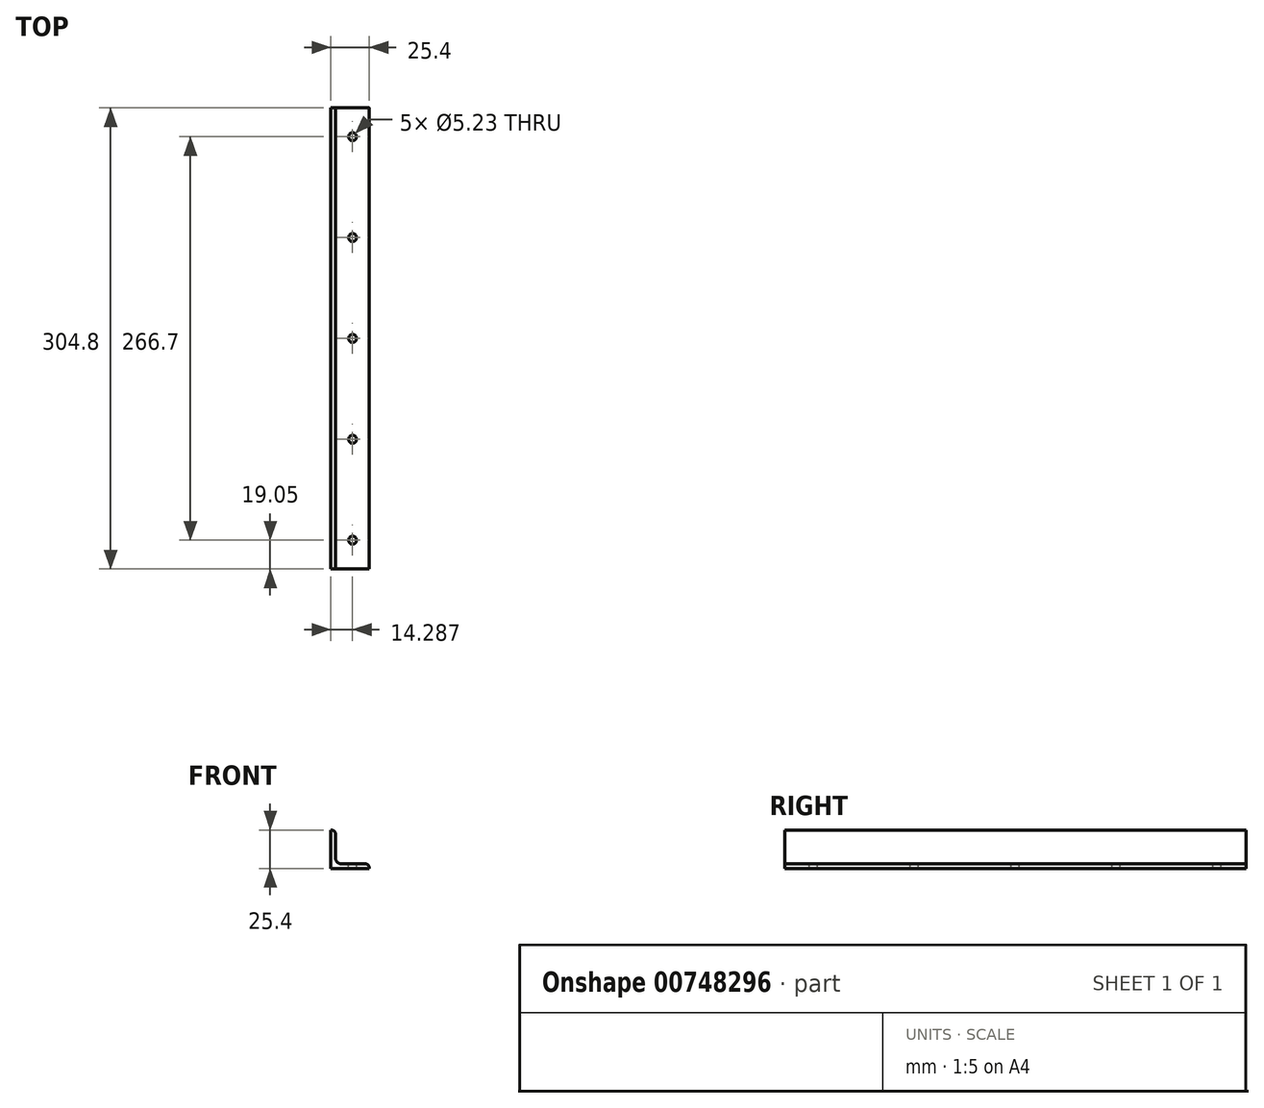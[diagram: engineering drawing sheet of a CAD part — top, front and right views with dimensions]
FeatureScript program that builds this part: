
annotation { "Feature Type Name" : "Feature", "Feature Type Description" : "" }
export const myFeature = defineFeature(function(context is Context, id is Id, definition is map)
    precondition{}
    {
        {
            var Q0;
            Q0=qCreatedBy(makeId("Front.planeOp"),FACE);
            var sketch = newSketch(context, id + "F0", { "sketchPlane" : qUnion([Q0])});
            skLineSegment(sketch, "E0", {"start": v(0, 0) * mm, "end": v(-25.4, 0) * mm});
            skLineSegment(sketch, "E1", {"start": v(-25.4, 0) * mm, "end": v(-25.4, 25.4) * mm});
            skLineSegment(sketch, "E2", {"start": v(-25.4, 25.4) * mm, "end": v(-25.4, 25.4) * mm});
            skLineSegment(sketch, "E3", {"start": v(-22.23, 22.23) * mm, "end": v(-22.23, 6.35) * mm});
            skLineSegment(sketch, "E4", {"start": v(-19.05, 3.18) * mm, "end": v(-3.18, 3.18) * mm});
            skLineSegment(sketch, "E5", {"start": v(0, 0) * mm, "end": v(0, 0) * mm});
            skPoint(sketch, "E6.visualSharp", {"position": v(-22.23, 3.18) * mm});
            skArc(sketch, "E6.filletArc", {"start": v(-22.23, 6.35) * mm, "mid": v(-21.3, 4.1) * mm, "end": v(-19.05, 3.18) * mm});
            skPoint(sketch, "E7.visualSharp", {"position": v(-22.23, 25.4) * mm});
            skArc(sketch, "E7.filletArc", {"start": v(-22.23, 22.23) * mm, "mid": v(-23.15, 24.47) * mm, "end": v(-25.4, 25.4) * mm});
            skPoint(sketch, "E8.visualSharp", {"position": v(0, 3.18) * mm});
            skArc(sketch, "E8.filletArc", {"start": v(0, 0) * mm, "mid": v(-0.93, 2.25) * mm, "end": v(-3.18, 3.18) * mm});
            skSolve(sketch);
        }
        {
            var Q0;
            Q0=qSketchRegion(id+"F0",true);
            extrude(context, id + "F1", {"entities" : qUnion([Q0]), "depth" : 304.8 * mm, "offsetDistance" : 25.4 * mm});
        }
        {
            var Q0;
            Q0=makeQuery(id+"F1.opExtrude","SWEPT_FACE",FACE,{"disambiguationData":[OSD([sQuery(id+"F0.wireOp",EDGE,"E4")])]});
            var sketch = newSketch(context, id + "F2", { "sketchPlane" : qUnion([Q0])});
            skLineSegment(sketch, "E9", {"start": v(-11.11, -304.8) * mm, "end": v(-11.11, 0) * mm, "construction": true});
            skCircle(sketch, "E10", {"center": v(-11.11, -285.75) * mm, "radius": 2.62 * mm});
            skCircle(sketch, "E11", {"center": v(-11.11, -19.05) * mm, "radius": 2.62 * mm});
            skCircle(sketch, "E12", {"center": v(-11.11, -219.07) * mm, "radius": 2.62 * mm});
            skCircle(sketch, "E13", {"center": v(-11.11, -152.4) * mm, "radius": 2.62 * mm});
            skCircle(sketch, "E14", {"center": v(-11.11, -85.72) * mm, "radius": 2.62 * mm});
            skSolve(sketch);
        }
        {
            var Q0;
            Q0=qSketchRegion(id+"F2",true);
            extrude(context, id + "F3", {"entities" : qUnion([Q0]), "operationType" : NewBodyOperationType.REMOVE, "endBound" : BoundingType.THROUGH_ALL, "oppositeDirection" : true, "depth" : 25.4 * mm, "offsetDistance" : 25.4 * mm});
        }
    });
